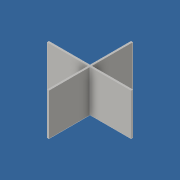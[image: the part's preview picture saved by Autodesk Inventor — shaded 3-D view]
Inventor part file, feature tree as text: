
AUTODESK INVENTOR PART (.ipt)
format: ipt  version: 2016 (Build 200138000, 138)  size: 80,384 bytes
history: native  units: in
note: dims shown in document units (in); Inventor stores cm internally (conversion verified against a paired STEP export)
features: extrude x1, sketch x1
ambient origin geometry x8: Origin, YZ Plane, XZ Plane, XY Plane, X Axis, Y Axis, Z Axis, Center Point
bodies: Solid1 (feature_tree)
feature tree (2):
  extrude  "Extrusion1"  Depth=0.02in
  sketch  "Sketch1"  dims[d0=1.0in d1=0.02in d2=1.0in d3=0.02in d4=0.5in d5=0.0in]
